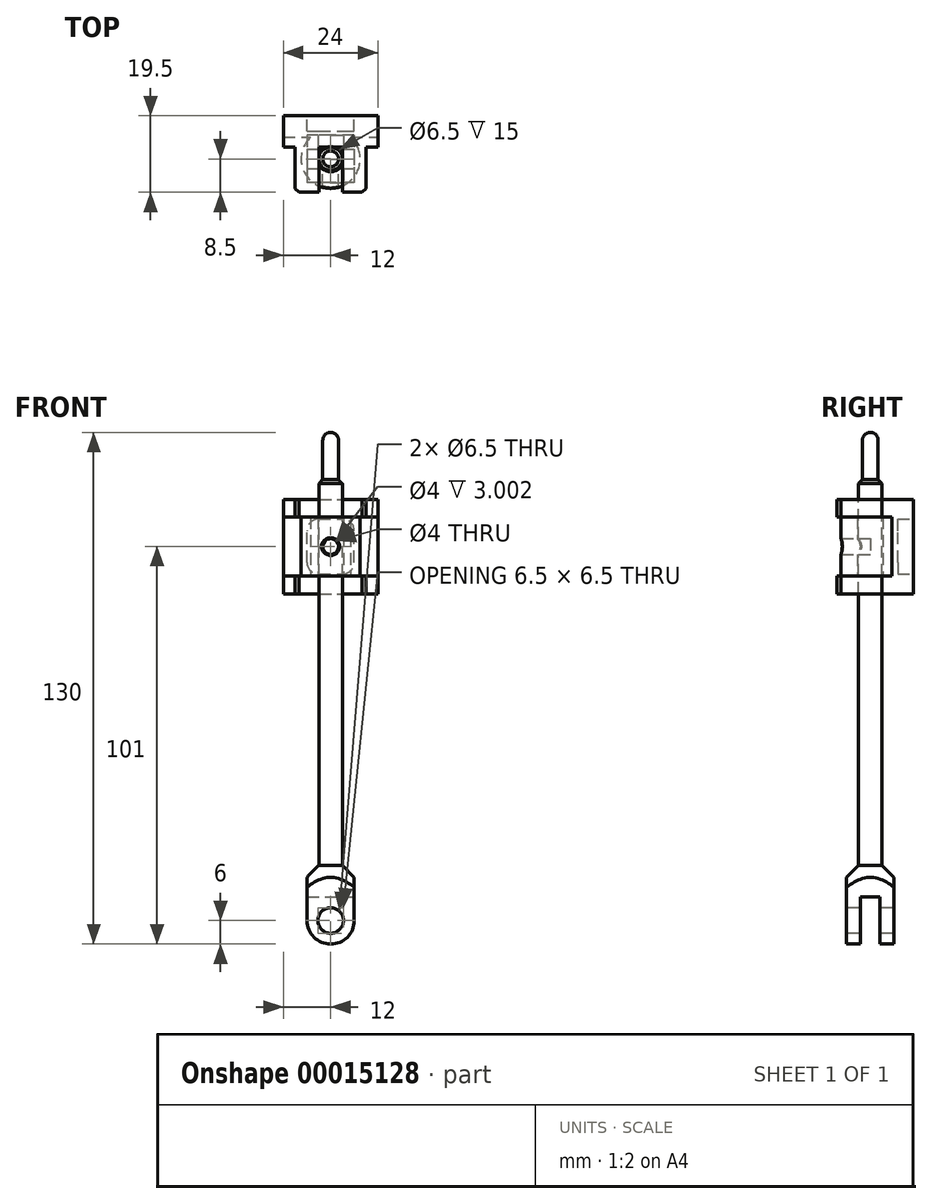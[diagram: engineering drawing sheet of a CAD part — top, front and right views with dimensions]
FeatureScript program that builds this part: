
annotation { "Feature Type Name" : "Feature", "Feature Type Description" : "" }
export const myFeature = defineFeature(function(context is Context, id is Id, definition is map)
    precondition{}
    {
        {
            var Q0;
            Q0=qCreatedBy(makeId("Top.planeOp"),FACE);
            cPlane(context, id + "F0", {"entities" : qUnion([Q0]), "cplaneType" : CPlaneType.OFFSET, "offset" : (124 - 12) * mm, "width" : 150 * mm, "height" : 150 * mm});
        }
        {
            var Q0;
            Q0=qCreatedBy(id+"F0.planeOp",FACE);
            var sketch = newSketch(context, id + "F1", { "sketchPlane" : qUnion([Q0])});
            skCircle(sketch, "E0", {"center": v(0, 0) * mm, "radius": 2 * mm});
            skCircle(sketch, "E1", {"center": v(0, 0) * mm, "radius": 3 * mm});
            skSolve(sketch);
        }
        {
            var Q0;
            Q0=makeQuery(id+"F1.imprint","IMPRINT",FACE,{"disambiguationData":[TD([[makeQuery(id+"F1.imprint","IMPRINT",EDGE,{"derivedFrom":sQuery(id+"F1.wireOp",EDGE,"E0")}),1.0]])]});
            extrude(context, id + "F2", {"entities" : qUnion([Q0]), "depth" : 12 * mm});
        }
        {
            var Q0;
            Q0=makeQuery(id+"F1.imprint","IMPRINT",FACE,{"disambiguationData":[TD([[makeQuery(id+"F1.imprint","IMPRINT",EDGE,{"derivedFrom":sQuery(id+"F1.wireOp",EDGE,"E0")}),1.0]])]});
            var Q1;
            Q1=makeQuery(id+"F1.imprint","IMPRINT",FACE,{"disambiguationData":[TD([[makeQuery(id+"F1.imprint","IMPRINT",EDGE,{"derivedFrom":sQuery(id+"F1.wireOp",EDGE,"E0")}),-1.0]])]});
            extrude(context, id + "F3", {"entities" : qUnion([Q0, Q1]), "operationType" : NewBodyOperationType.ADD, "oppositeDirection" : true, "depth" : 98 * mm});
        }
        {
            var Q0;
            Q0=makeQuery(id+"F3.opExtrude","CAP_FACE",FACE,{"disambiguationData":[OSD([sQuery(id+"F1.wireOp",EDGE,"E1")])],"isStart":false});
            var sketch = newSketch(context, id + "F4", { "sketchPlane" : qUnion([Q0])});
            skLineSegment(sketch, "E2.rect.bottom", {"start": v(6, -6) * mm, "end": v(-6, -6) * mm});
            skLineSegment(sketch, "E2.rect.top", {"start": v(6, 6) * mm, "end": v(-6, 6) * mm});
            skLineSegment(sketch, "E2.rect.left", {"start": v(6, -6) * mm, "end": v(6, 6) * mm});
            skLineSegment(sketch, "E2.rect.right", {"start": v(-6, -6) * mm, "end": v(-6, 6) * mm});
            skPoint(sketch, "E2.rect.middle", {"position": v(0, 0) * mm});
            skSolve(sketch);
        }
        {
            var Q0;
            Q0=makeQuery(id+"F4.imprint","IMPRINT",FACE,{"disambiguationData":[TD([[makeQuery(id+"F4.imprint","IMPRINT",EDGE,{"derivedFrom":makeQuery(id+"F3.opExtrude","CAP_EDGE",EDGE,{"disambiguationData":[OSD([sQuery(id+"F1.wireOp",EDGE,"E1")])],"isStart":false})}),-1.0]])]});
            var Q1;
            Q1=makeQuery(id+"F4.imprint","IMPRINT",FACE,{"disambiguationData":[TD([[makeQuery(id+"F4.imprint","IMPRINT",EDGE,{"derivedFrom":sQuery(id+"F4.wireOp",EDGE,"E2.rect.bottom")}),-1.0]])]});
            extrude(context, id + "F5", {"entities" : qUnion([Q0, Q1]), "operationType" : NewBodyOperationType.ADD, "depth" : (124 - 12 - 98 + 6) * mm});
        }
        {
            var Q0;
            Q0=makeQuery(id+"F2.opExtrude","CAP_EDGE",EDGE,{"disambiguationData":[OSD([sQuery(id+"F1.wireOp",EDGE,"E0")])],"isStart":false});
            fillet(context, id + "F6", {"entities" : qUnion([Q0]), "radius" : 2 * mm, "tangentPropagation" : true, "allowEdgeOverflow" : false});
        }
        {
            var Q0;
            Q0=makeQuery(id+"F3.opExtrude","CAP_EDGE",EDGE,{"disambiguationData":[OSD([sQuery(id+"F1.wireOp",EDGE,"E1")])],"isStart":true});
            chamfer(context, id + "F7", {"entities" : qUnion([Q0]), "width" : 1 * mm, "tangentPropagation" : true});
        }
        {
            var Q0;
            Q0=qCreatedBy(makeId("Front.planeOp"),FACE);
            var sketch = newSketch(context, id + "F8", { "sketchPlane" : qUnion([Q0])});
            skLineSegment(sketch, "E3", {"start": v(3, 111) * mm, "end": v(3, 14) * mm});
            skLineSegment(sketch, "E4", {"start": v(-3, 14) * mm, "end": v(-3, 111) * mm});
            skLineSegment(sketch, "E5.0.0", {"start": v(6, 14) * mm, "end": v(-6, 14) * mm});
            skLineSegment(sketch, "E5.0.1", {"start": v(-6, 14) * mm, "end": v(-6, -6) * mm});
            skLineSegment(sketch, "E5.0.2", {"start": v(-6, -6) * mm, "end": v(6, -6) * mm});
            skLineSegment(sketch, "E5.0.3", {"start": v(6, -6) * mm, "end": v(6, 14) * mm});
            skLineSegment(sketch, "E6", {"start": v(3, 14) * mm, "end": v(10.82, 6.18) * mm});
            skLineSegment(sketch, "E7", {"start": v(10.82, 6.18) * mm, "end": v(10.82, 14) * mm});
            skLineSegment(sketch, "E8", {"start": v(10.82, 14) * mm, "end": v(3, 14) * mm});
            skLineSegment(sketch, "E9", {"start": v(0, 14) * mm, "end": v(0, -10.92) * mm, "construction": true});
            skSolve(sketch);
        }
        {
            var Q0;
            {var subQ1=sQuery(id+"F8.wireOp",EDGE,"E7");Q0=makeQuery(id+"F8.imprint","IMPRINT",FACE,{"disambiguationData":[TD([[makeQuery(id+"F8.imprint","IMPRINT",EDGE,{"derivedFrom":subQ1}),1.0]])]});}
            var Q1;
            {var subQ0=sQuery(id+"F8.wireOp",EDGE,"E8");var subQ1=sQuery(id+"F8.wireOp",EDGE,"E5.0.3");var subQ2=makeQuery(id+"F8.imprint","INTERSECT",VERTEX,{"derivedFrom":[subQ1,subQ0]});Q1=makeQuery(id+"F8.imprint","IMPRINT",FACE,{"disambiguationData":[TD([[makeQuery(id+"F8.imprint","IMPRINT",EDGE,{"disambiguationData":[TD([[subQ2,1.0]])],"derivedFrom":subQ1}),1.0]])]});}
            var Q2;
            Q2=sQuery(id+"F8.wireOp",EDGE,"E9");
            revolve(context, id + "F9", {"operationType" : NewBodyOperationType.REMOVE, "entities" : qUnion([Q0, Q1]), "axis" : qUnion([Q2]), "revolveType" : RevolveType.FULL, "oppositeDirection" : true});
        }
        {
            var Q0;
            Q0=qCreatedBy(makeId("Front.planeOp"),FACE);
            var sketch = newSketch(context, id + "F10", { "sketchPlane" : qUnion([Q0])});
            skLineSegment(sketch, "E10", {"start": v(0, 25.93) * mm, "end": v(0, -19.45) * mm, "construction": true});
            skCircle(sketch, "E11", {"center": v(0, 0) * mm, "radius": 3.25 * mm});
            skArc(sketch, "E12", {"start": v(2, 122) * mm, "mid": v(0, 124) * mm, "end": v(-2, 122) * mm});
            skCircle(sketch, "E13", {"center": v(0, 0) * mm, "radius": 6 * mm});
            skLineSegment(sketch, "E14.0", {"start": v(6, -6) * mm, "end": v(-6, -6) * mm});
            skLineSegment(sketch, "E15.0", {"start": v(6, -6) * mm, "end": v(6, 8.51) * mm});
            skLineSegment(sketch, "E16.0", {"start": v(-6, -6) * mm, "end": v(-6, 8.51) * mm});
            skSolve(sketch);
        }
        {
            var Q0;
            Q0=makeQuery(id+"F10.imprint","IMPRINT",FACE,{"disambiguationData":[TD([[makeQuery(id+"F10.imprint","IMPRINT",EDGE,{"derivedFrom":sQuery(id+"F10.wireOp",EDGE,"E11")}),1.0]])]});
            var Q1;
            {var subQ0=sQuery(id+"F10.wireOp",EDGE,"E15.0");var subQ1=sQuery(id+"F10.wireOp",EDGE,"E13");var subQ2=makeQuery(id+"F10.imprint","INTERSECT",VERTEX,{"derivedFrom":[subQ1,subQ0]});Q1=makeQuery(id+"F10.imprint","IMPRINT",FACE,{"disambiguationData":[TD([[makeQuery(id+"F10.imprint","IMPRINT",EDGE,{"disambiguationData":[TD([[subQ2,1.0]])],"derivedFrom":subQ1}),-1.0]])]});}
            var Q2;
            {var subQ0=sQuery(id+"F10.wireOp",EDGE,"E16.0");var subQ1=sQuery(id+"F10.wireOp",EDGE,"E13");var subQ2=makeQuery(id+"F10.imprint","INTERSECT",VERTEX,{"derivedFrom":[subQ1,subQ0]});Q2=makeQuery(id+"F10.imprint","IMPRINT",FACE,{"disambiguationData":[TD([[makeQuery(id+"F10.imprint","IMPRINT",EDGE,{"disambiguationData":[TD([[subQ2,-1.0]])],"derivedFrom":subQ1}),-1.0]])]});}
            extrude(context, id + "F11", {"entities" : qUnion([Q0, Q1, Q2]), "operationType" : NewBodyOperationType.REMOVE, "endBound" : BoundingType.THROUGH_ALL, "oppositeDirection" : true, "depth" : 25 * mm, "hasSecondDirection" : true, "secondDirectionBound" : SecondDirectionBoundingType.THROUGH_ALL, "secondDirectionOppositeDirection" : false, "secondDirectionDepth" : 25 * mm});
        }
        {
            var Q0;
            Q0=qCreatedBy(makeId("Right.planeOp"),FACE);
            var sketch = newSketch(context, id + "F12", { "sketchPlane" : qUnion([Q0])});
            skLineSegment(sketch, "E17", {"start": v(0, -8.1) * mm, "end": v(0, 19.8) * mm, "construction": true});
            skLineSegment(sketch, "E18.bottom", {"start": v(-2.5, 6) * mm, "end": v(2.5, 6) * mm});
            skLineSegment(sketch, "E18.top", {"start": v(-2.5, -12.9) * mm, "end": v(2.5, -12.9) * mm});
            skLineSegment(sketch, "E18.left", {"start": v(-2.5, 6) * mm, "end": v(-2.5, -12.9) * mm});
            skLineSegment(sketch, "E18.right", {"start": v(2.5, 6) * mm, "end": v(2.5, -12.9) * mm});
            skLineSegment(sketch, "E19", {"start": v(6, -6) * mm, "end": v(-6, -6) * mm});
            skSolve(sketch);
        }
        {
            var Q0;
            {var subQ5=sQuery(id+"F12.wireOp",EDGE,"E18.bottom");Q0=makeQuery(id+"F12.imprint","IMPRINT",FACE,{"disambiguationData":[TD([[makeQuery(id+"F12.imprint","IMPRINT",EDGE,{"derivedFrom":subQ5}),-1.0]])]});}
            var Q1;
            {var subQ5=sQuery(id+"F12.wireOp",EDGE,"E18.top");Q1=makeQuery(id+"F12.imprint","IMPRINT",FACE,{"disambiguationData":[TD([[makeQuery(id+"F12.imprint","IMPRINT",EDGE,{"derivedFrom":subQ5}),1.0]])]});}
            extrude(context, id + "F13", {"entities" : qUnion([Q0, Q1]), "operationType" : NewBodyOperationType.REMOVE, "endBound" : BoundingType.THROUGH_ALL, "oppositeDirection" : true, "depth" : 25 * mm, "hasSecondDirection" : true, "secondDirectionBound" : SecondDirectionBoundingType.THROUGH_ALL, "secondDirectionOppositeDirection" : false, "secondDirectionDepth" : 25 * mm});
        }
        {
            var Q0;
            Q0=qCreatedBy(makeId("Top.planeOp"),FACE);
            cPlane(context, id + "F14", {"entities" : qUnion([Q0]), "cplaneType" : CPlaneType.OFFSET, "offset" : 95 * mm, "width" : 150 * mm, "height" : 150 * mm});
        }
        {
            var Q0;
            Q0=qCreatedBy(id+"F14.planeOp",FACE);
            var sketch = newSketch(context, id + "F15", { "sketchPlane" : qUnion([Q0])});
            skPoint(sketch, "E20.0", {"position": v(0, 0) * mm});
            skArc(sketch, "E21", {"start": v(-5.1, 5.5) * mm, "mid": v(0, -7.5) * mm, "end": v(5.1, 5.5) * mm});
            skCircle(sketch, "E22", {"center": v(0, 0) * mm, "radius": 3.25 * mm});
            skCircle(sketch, "E23.0", {"center": v(0, 0) * mm, "radius": 2 * mm, "construction": true});
            skLineSegment(sketch, "E24", {"start": v(-5.1, 5.5) * mm, "end": v(5.1, 5.5) * mm});
            skSolve(sketch);
        }
        {
            var Q0;
            Q0=qSketchRegion(id+"F15",true);
            extrude(context, id + "F16", {"entities" : qUnion([Q0]), "endBound" : BoundingType.SYMMETRIC, "depth" : 15 * mm});
        }
        {
            var Q0;
            Q0=qCreatedBy(makeId("Front.planeOp"),FACE);
            var sketch = newSketch(context, id + "F17", { "sketchPlane" : qUnion([Q0])});
            skLineSegment(sketch, "E25", {"start": v(0, 91.37) * mm, "end": v(0, 113.25) * mm, "construction": true});
            skLineSegment(sketch, "E26", {"start": v(-7.5, 87.5) * mm, "end": v(-7.5, 102.5) * mm});
            skLineSegment(sketch, "E27", {"start": v(7.5, 102.5) * mm, "end": v(7.5, 87.5) * mm});
            skCircle(sketch, "E28", {"center": v(0, 95) * mm, "radius": 2 * mm});
            skLineSegment(sketch, "E29", {"start": v(-7.5, 95) * mm, "end": v(7.5, 95) * mm, "construction": true});
            skLineSegment(sketch, "E30.0", {"start": v(-7.5, 87.5) * mm, "end": v(7.5, 87.5) * mm});
            skLineSegment(sketch, "E31.0", {"start": v(-7.5, 102.5) * mm, "end": v(7.5, 102.5) * mm});
            skSolve(sketch);
        }
        {
            var Q0;
            Q0=makeQuery(id+"F17.imprint","IMPRINT",FACE,{"disambiguationData":[TD([[makeQuery(id+"F17.imprint","IMPRINT",EDGE,{"derivedFrom":sQuery(id+"F17.wireOp",EDGE,"E28")}),1.0]])]});
            extrude(context, id + "F18", {"entities" : qUnion([Q0]), "operationType" : NewBodyOperationType.REMOVE, "endBound" : BoundingType.THROUGH_ALL, "depth" : 25 * mm});
        }
        {
            var Q0;
            Q0=makeQuery(id+"F18.boolean.opBoolean","INTERSECT",EDGE,{"derivedFrom":[makeQuery(id+"F16.opExtrude","SWEPT_FACE",FACE,{"disambiguationData":[OSD([sQuery(id+"F15.wireOp",EDGE,"E21")])]}),makeQuery(id+"F18.opExtrude","SWEPT_FACE",FACE,{"disambiguationData":[OSD([sQuery(id+"F17.wireOp",EDGE,"E28")])]})]});
            chamfer(context, id + "F19", {"entities" : qUnion([Q0]), "width" : .25 * mm, "tangentPropagation" : true});
        }
        {
            var Q0;
            Q0=makeQuery(id+"F16.opExtrude","SWEPT_FACE",FACE,{"disambiguationData":[OSD([sQuery(id+"F15.wireOp",EDGE,"E24")])]});
            var sketch = newSketch(context, id + "F20", { "sketchPlane" : qUnion([Q0])});
            skLineSegment(sketch, "E32.0.0", {"start": v(-5.1, 87.5) * mm, "end": v(5.1, 87.5) * mm});
            skLineSegment(sketch, "E32.0.1", {"start": v(5.1, 87.5) * mm, "end": v(5.1, 102.5) * mm});
            skLineSegment(sketch, "E32.0.2", {"start": v(5.1, 102.5) * mm, "end": v(-5.1, 102.5) * mm});
            skLineSegment(sketch, "E32.0.3", {"start": v(-5.1, 102.5) * mm, "end": v(-5.1, 87.5) * mm});
            skLineSegment(sketch, "E33", {"start": v(0, 102.5) * mm, "end": v(0, 87.5) * mm, "construction": true});
            skLineSegment(sketch, "E34", {"start": v(5.1, 95) * mm, "end": v(-5.1, 95) * mm, "construction": true});
            skLineSegment(sketch, "E35.rect.bottom", {"start": v(12, 83) * mm, "end": v(-12, 83) * mm});
            skLineSegment(sketch, "E35.rect.top", {"start": v(12, 107) * mm, "end": v(-12, 107) * mm});
            skLineSegment(sketch, "E35.rect.left", {"start": v(12, 83) * mm, "end": v(12, 107) * mm});
            skLineSegment(sketch, "E35.rect.right", {"start": v(-12, 83) * mm, "end": v(-12, 107) * mm});
            skPoint(sketch, "E35.rect.middle", {"position": v(0, 95) * mm});
            skLineSegment(sketch, "E36.rect.bottom", {"start": v(12, 87.5) * mm, "end": v(-12, 87.5) * mm});
            skLineSegment(sketch, "E36.rect.top", {"start": v(12, 102.5) * mm, "end": v(-12, 102.5) * mm});
            skLineSegment(sketch, "E36.rect.left", {"start": v(12, 87.5) * mm, "end": v(12, 102.5) * mm});
            skLineSegment(sketch, "E36.rect.right", {"start": v(-12, 87.5) * mm, "end": v(-12, 102.5) * mm});
            skSolve(sketch);
        }
        {
            var Q0;
            {var subQ7=sQuery(id+"F20.wireOp",EDGE,"E35.rect.top");Q0=makeQuery(id+"F20.imprint","IMPRINT",FACE,{"disambiguationData":[TD([[makeQuery(id+"F20.imprint","IMPRINT",EDGE,{"derivedFrom":subQ7}),1.0]])]});}
            var Q1;
            {var subQ3=sQuery(id+"F20.wireOp",EDGE,"E32.0.1");Q1=makeQuery(id+"F20.imprint","IMPRINT",FACE,{"disambiguationData":[TD([[makeQuery(id+"F20.imprint","IMPRINT",EDGE,{"derivedFrom":subQ3}),1.0]])]});}
            var Q2;
            {var subQ2=sQuery(id+"F20.wireOp",EDGE,"E32.0.1");Q2=makeQuery(id+"F20.imprint","IMPRINT",FACE,{"disambiguationData":[TD([[makeQuery(id+"F20.imprint","IMPRINT",EDGE,{"derivedFrom":subQ2}),-1.0]])]});}
            var Q3;
            {var subQ3=sQuery(id+"F20.wireOp",EDGE,"E32.0.3");Q3=makeQuery(id+"F20.imprint","IMPRINT",FACE,{"disambiguationData":[TD([[makeQuery(id+"F20.imprint","IMPRINT",EDGE,{"derivedFrom":subQ3}),-1.0]])]});}
            var Q4;
            {var subQ7=sQuery(id+"F20.wireOp",EDGE,"E35.rect.bottom");Q4=makeQuery(id+"F20.imprint","IMPRINT",FACE,{"disambiguationData":[TD([[makeQuery(id+"F20.imprint","IMPRINT",EDGE,{"derivedFrom":subQ7}),-1.0]])]});}
            extrude(context, id + "F21", {"entities" : qUnion([Q0, Q1, Q2, Q3, Q4]), "depth" : (19.5 - 14) * mm});
        }
        {
            var Q0;
            {var subQ7=sQuery(id+"F20.wireOp",EDGE,"E35.rect.top");Q0=makeQuery(id+"F20.imprint","IMPRINT",FACE,{"disambiguationData":[TD([[makeQuery(id+"F20.imprint","IMPRINT",EDGE,{"derivedFrom":subQ7}),1.0]])]});}
            var Q1;
            {var subQ7=sQuery(id+"F20.wireOp",EDGE,"E35.rect.bottom");Q1=makeQuery(id+"F20.imprint","IMPRINT",FACE,{"disambiguationData":[TD([[makeQuery(id+"F20.imprint","IMPRINT",EDGE,{"derivedFrom":subQ7}),-1.0]])]});}
            extrude(context, id + "F22", {"entities" : qUnion([Q0, Q1]), "operationType" : NewBodyOperationType.ADD, "oppositeDirection" : true, "depth" : (14 - 11.5) * mm});
        }
        {
            var Q0;
            Q0=makeQuery(id+"F22.opExtrude","CAP_FACE",FACE,{"disambiguationData":[OSD([sQuery(id+"F20.wireOp",EDGE,"E35.rect.top"),sQuery(id+"F20.wireOp",EDGE,"E35.rect.left"),sQuery(id+"F20.wireOp",EDGE,"E35.rect.right"),sQuery(id+"F20.wireOp",EDGE,"E36.rect.top")])],"isStart":false});
            var sketch = newSketch(context, id + "F23", { "sketchPlane" : qUnion([Q0])});
            skLineSegment(sketch, "E37.0.0", {"start": v(-12, 107) * mm, "end": v(-12, 102.5) * mm, "construction": true});
            skLineSegment(sketch, "E37.0.1", {"start": v(-12, 102.5) * mm, "end": v(12, 102.5) * mm, "construction": true});
            skLineSegment(sketch, "E37.0.2", {"start": v(12, 102.5) * mm, "end": v(12, 107) * mm, "construction": true});
            skLineSegment(sketch, "E37.0.3", {"start": v(12, 107) * mm, "end": v(-12, 107) * mm, "construction": true});
            skLineSegment(sketch, "E38.0.0", {"start": v(-12, 83) * mm, "end": v(12, 83) * mm, "construction": true});
            skLineSegment(sketch, "E38.0.1", {"start": v(12, 83) * mm, "end": v(12, 87.5) * mm, "construction": true});
            skLineSegment(sketch, "E38.0.2", {"start": v(12, 87.5) * mm, "end": v(-12, 87.5) * mm, "construction": true});
            skLineSegment(sketch, "E38.0.3", {"start": v(-12, 87.5) * mm, "end": v(-12, 83) * mm, "construction": true});
            skLineSegment(sketch, "E39.0", {"start": v(-12, 83) * mm, "end": v(-12, 107) * mm, "construction": true});
            skLineSegment(sketch, "E40.0", {"start": v(12, 83) * mm, "end": v(12, 107) * mm, "construction": true});
            skLineSegment(sketch, "E41", {"start": v(0, 107) * mm, "end": v(0, 83) * mm, "construction": true});
            skLineSegment(sketch, "E42.0", {"start": v(-12, 87.5) * mm, "end": v(12, 87.5) * mm});
            skLineSegment(sketch, "E43.0", {"start": v(-12, 102.5) * mm, "end": v(12, 102.5) * mm});
            skLineSegment(sketch, "E44.0", {"start": v(-12, 107) * mm, "end": v(12, 107) * mm});
            skLineSegment(sketch, "E45", {"start": v(12, 95) * mm, "end": v(-12, 95) * mm, "construction": true});
            skLineSegment(sketch, "E46.bottom", {"start": v(3, 107) * mm, "end": v(9, 107) * mm});
            skLineSegment(sketch, "E46.top", {"start": v(3, 102.5) * mm, "end": v(9, 102.5) * mm});
            skLineSegment(sketch, "E46.left", {"start": v(3, 107) * mm, "end": v(3, 102.5) * mm});
            skLineSegment(sketch, "E46.right", {"start": v(9, 107) * mm, "end": v(9, 102.5) * mm});
            skLineSegment(sketch, "E47.0.MirrorCS", {"start": v(-3, 107) * mm, "end": v(-3, 102.5) * mm});
            skLineSegment(sketch, "E48.0.MirrorCS", {"start": v(-9, 107) * mm, "end": v(-9, 102.5) * mm});
            skLineSegment(sketch, "E49.0.MirrorCS", {"start": v(12, 107) * mm, "end": v(-12, 107) * mm});
            skLineSegment(sketch, "E50.0.MirrorCS", {"start": v(12, 102.5) * mm, "end": v(-12, 102.5) * mm});
            skLineSegment(sketch, "E51.0.MirrorCS", {"start": v(9, 83) * mm, "end": v(9, 87.5) * mm});
            skLineSegment(sketch, "E52.0.MirrorCS", {"start": v(3, 83) * mm, "end": v(3, 87.5) * mm});
            skLineSegment(sketch, "E53.0.MirrorCS", {"start": v(-3, 83) * mm, "end": v(-3, 87.5) * mm});
            skLineSegment(sketch, "E54.0.MirrorCS", {"start": v(-9, 83) * mm, "end": v(-9, 87.5) * mm});
            skLineSegment(sketch, "E55", {"start": v(12, 87.5) * mm, "end": v(-12, 87.5) * mm});
            skLineSegment(sketch, "E56", {"start": v(-12, 83) * mm, "end": v(12, 83) * mm});
            skSolve(sketch);
        }
        {
            var Q0;
            {var subQ2=sQuery(id+"F23.wireOp",EDGE,"E47.0.MirrorCS");Q0=makeQuery(id+"F23.imprint","IMPRINT",FACE,{"disambiguationData":[TD([[makeQuery(id+"F23.imprint","IMPRINT",EDGE,{"derivedFrom":subQ2}),-1.0]])]});}
            var Q1;
            {var subQ2=sQuery(id+"F23.wireOp",EDGE,"E46.left");Q1=makeQuery(id+"F23.imprint","IMPRINT",FACE,{"disambiguationData":[TD([[makeQuery(id+"F23.imprint","IMPRINT",EDGE,{"derivedFrom":subQ2}),1.0]])]});}
            var Q2;
            {var subQ2=sQuery(id+"F23.wireOp",EDGE,"E53.0.MirrorCS");Q2=makeQuery(id+"F23.imprint","IMPRINT",FACE,{"disambiguationData":[TD([[makeQuery(id+"F23.imprint","IMPRINT",EDGE,{"derivedFrom":subQ2}),1.0]])]});}
            var Q3;
            {var subQ2=sQuery(id+"F23.wireOp",EDGE,"E51.0.MirrorCS");Q3=makeQuery(id+"F23.imprint","IMPRINT",FACE,{"disambiguationData":[TD([[makeQuery(id+"F23.imprint","IMPRINT",EDGE,{"derivedFrom":subQ2}),1.0]])]});}
            extrude(context, id + "F24", {"entities" : qUnion([Q0, Q1, Q2, Q3]), "operationType" : NewBodyOperationType.ADD, "depth" : 11.5 * mm});
        }
        {
            var Q0;
            Q0=makeQuery(id+"F24.opExtrude","CAP_EDGE",EDGE,{"disambiguationData":[OSD([sQuery(id+"F23.wireOp",EDGE,"E48.0.MirrorCS")])],"isStart":false});
            var Q1;
            Q1=makeQuery(id+"F24.opExtrude","CAP_EDGE",EDGE,{"disambiguationData":[OSD([sQuery(id+"F23.wireOp",EDGE,"E54.0.MirrorCS")])],"isStart":false});
            var Q2;
            Q2=makeQuery(id+"F24.opExtrude","CAP_EDGE",EDGE,{"disambiguationData":[OSD([sQuery(id+"F23.wireOp",EDGE,"E46.right")])],"isStart":false});
            var Q3;
            Q3=makeQuery(id+"F24.opExtrude","CAP_EDGE",EDGE,{"disambiguationData":[OSD([sQuery(id+"F23.wireOp",EDGE,"E51.0.MirrorCS")])],"isStart":false});
            chamfer(context, id + "F25", {"entities" : qUnion([Q0, Q1, Q2, Q3]), "width" : 1 * mm, "tangentPropagation" : true});
        }
        {
            var Q0;
            Q0=makeQuery(id+"F21.opExtrude","CAP_FACE",FACE,{"disambiguationData":[OSD([sQuery(id+"F20.wireOp",EDGE,"E35.rect.bottom"),sQuery(id+"F20.wireOp",EDGE,"E35.rect.top"),sQuery(id+"F20.wireOp",EDGE,"E35.rect.left"),sQuery(id+"F20.wireOp",EDGE,"E35.rect.right"),sQuery(id+"F20.wireOp",EDGE,"E36.rect.left"),sQuery(id+"F20.wireOp",EDGE,"E36.rect.right")])],"isStart":false});
            var sketch = newSketch(context, id + "F26", { "sketchPlane" : qUnion([Q0])});
            skLineSegment(sketch, "E57.0", {"start": v(0, 102.5) * mm, "end": v(0, 87.5) * mm, "construction": true});
            skLineSegment(sketch, "E58.0", {"start": v(5.1, 95) * mm, "end": v(-5.1, 95) * mm, "construction": true});
            skLineSegment(sketch, "E59.rect.bottom", {"start": v(3, 88) * mm, "end": v(-3, 88) * mm});
            skLineSegment(sketch, "E59.rect.top", {"start": v(3, 102) * mm, "end": v(-3, 102) * mm});
            skLineSegment(sketch, "E59.rect.left", {"start": v(6, 91) * mm, "end": v(6, 99) * mm});
            skLineSegment(sketch, "E59.rect.right", {"start": v(-6, 91) * mm, "end": v(-6, 99) * mm});
            skPoint(sketch, "E59.rect.middle", {"position": v(0, 95) * mm});
            skPoint(sketch, "E60.visualSharp", {"position": v(-6, 102) * mm});
            skArc(sketch, "E60.filletArc", {"start": v(-3, 102) * mm, "mid": v(-5.12, 101.12) * mm, "end": v(-6, 99) * mm});
            skPoint(sketch, "E61.visualSharp", {"position": v(6, 102) * mm});
            skArc(sketch, "E61.filletArc", {"start": v(6, 99) * mm, "mid": v(5.12, 101.12) * mm, "end": v(3, 102) * mm});
            skPoint(sketch, "E62.visualSharp", {"position": v(6, 88) * mm});
            skArc(sketch, "E62.filletArc", {"start": v(3, 88) * mm, "mid": v(5.12, 88.88) * mm, "end": v(6, 91) * mm});
            skPoint(sketch, "E63.visualSharp", {"position": v(-6, 88) * mm});
            skArc(sketch, "E63.filletArc", {"start": v(-6, 91) * mm, "mid": v(-5.12, 88.88) * mm, "end": v(-3, 88) * mm});
            skSolve(sketch);
        }
        {
            var Q0;
            Q0=makeQuery(id+"F26.imprint","IMPRINT",FACE,{"disambiguationData":[TD([[makeQuery(id+"F26.imprint","IMPRINT",EDGE,{"derivedFrom":sQuery(id+"F26.wireOp",EDGE,"E59.rect.bottom")}),-1.0]])]});
            extrude(context, id + "F27", {"entities" : qUnion([Q0]), "operationType" : NewBodyOperationType.REMOVE, "oppositeDirection" : true, "depth" : 4 * mm});
        }
    });
